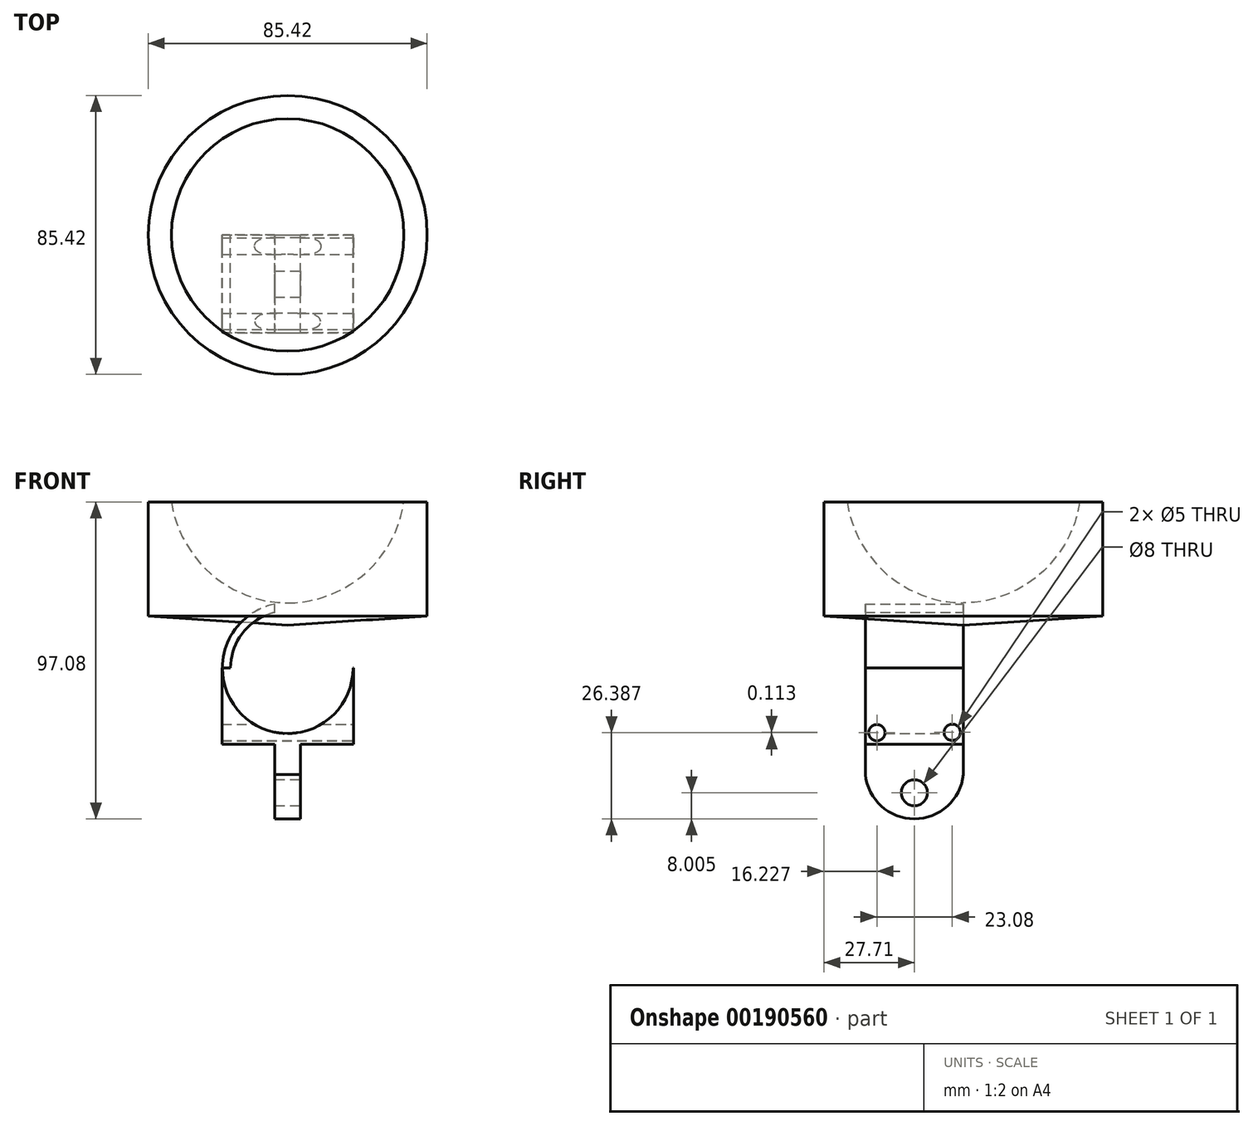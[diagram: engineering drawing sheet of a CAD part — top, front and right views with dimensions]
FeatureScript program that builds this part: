
annotation { "Feature Type Name" : "Feature", "Feature Type Description" : "" }
export const myFeature = defineFeature(function(context is Context, id is Id, definition is map)
    precondition{}
    {
        {
            var Q0;
            Q0=qCreatedBy(makeId("Front.planeOp"),FACE);
            var sketch = newSketch(context, id + "F0", { "sketchPlane" : qUnion([Q0])});
            skCircle(sketch, "E0", {"center": v(0, 0) * mm, "radius": 17.5 * mm});
            skLineSegment(sketch, "E1.bottom", {"start": v(3.9, -46.27) * mm, "end": v(-3.9, -46.27) * mm});
            skLineSegment(sketch, "E1.top", {"start": v(3.9, 46.27) * mm, "end": v(-3.9, 46.27) * mm});
            skLineSegment(sketch, "E1.left", {"start": v(3.9, -46.27) * mm, "end": v(3.9, 46.27) * mm});
            skLineSegment(sketch, "E1.right", {"start": v(-3.9, -46.27) * mm, "end": v(-3.9, 46.27) * mm});
            skCircle(sketch, "E2", {"center": v(0, 0) * mm, "radius": 20 * mm});
            skLineSegment(sketch, "E3.bottom", {"start": v(20.14, -23.25) * mm, "end": v(-20.14, -23.25) * mm});
            skLineSegment(sketch, "E3.top", {"start": v(20.14, 23.25) * mm, "end": v(-20.14, 23.25) * mm});
            skLineSegment(sketch, "E3.left", {"start": v(20.14, -23.25) * mm, "end": v(20.14, 23.25) * mm});
            skLineSegment(sketch, "E3.right", {"start": v(-20.14, -23.25) * mm, "end": v(-20.14, 23.25) * mm});
            skLineSegment(sketch, "E4", {"start": v(-17.5, 0) * mm, "end": v(20, 0) * mm});
            skPoint(sketch, "E4.startSnap0", {"position": v(-20.14, 0) * mm});
            skLineSegment(sketch, "E5", {"start": v(-20.14, 0) * mm, "end": v(20, 0) * mm});
            skLineSegment(sketch, "E6", {"start": v(25.02, 0) * mm, "end": v(-25.66, 0) * mm});
            skSolve(sketch);
        }
        {
            var Q0;
            {var subQ1=sQuery(id+"F0.wireOp",EDGE,"E3.bottom");var subQ5=sQuery(id+"F0.wireOp",EDGE,"E1.left");var subQ6=makeQuery(id+"F0.imprint","INTERSECT",VERTEX,{"derivedFrom":[subQ5,subQ1]});Q0=makeQuery(id+"F0.imprint","IMPRINT",FACE,{"disambiguationData":[TD([[makeQuery(id+"F0.imprint","IMPRINT",EDGE,{"disambiguationData":[TD([[subQ6,-1.0]])],"derivedFrom":subQ5}),-1.0]])]});}
            var Q1;
            {var subQ0=sQuery(id+"F0.wireOp",EDGE,"E6");var subQ1=sQuery(id+"F0.wireOp",EDGE,"E0");var subQ2=makeQuery(id+"F0.imprint","INTERSECT",VERTEX,{"disambiguationData":[OD(0.0)],"derivedFrom":[subQ1,subQ0]});Q1=makeQuery(id+"F0.imprint","IMPRINT",FACE,{"disambiguationData":[TD([[makeQuery(id+"F0.imprint","IMPRINT",EDGE,{"disambiguationData":[TD([[subQ2,1.0]])],"derivedFrom":subQ1}),-1.0]])]});}
            var Q2;
            {var subQ0=sQuery(id+"F0.wireOp",EDGE,"E1.right");var subQ1=sQuery(id+"F0.wireOp",EDGE,"E0");var subQ2=makeQuery(id+"F0.imprint","INTERSECT",VERTEX,{"disambiguationData":[OD(1.0)],"derivedFrom":[subQ1,subQ0]});Q2=makeQuery(id+"F0.imprint","IMPRINT",FACE,{"disambiguationData":[TD([[makeQuery(id+"F0.imprint","IMPRINT",EDGE,{"disambiguationData":[TD([[subQ2,-1.0]])],"derivedFrom":subQ1}),-1.0]])]});}
            var Q3;
            {var subQ0=sQuery(id+"F0.wireOp",EDGE,"E6");var subQ1=sQuery(id+"F0.wireOp",EDGE,"E0");var subQ2=makeQuery(id+"F0.imprint","INTERSECT",VERTEX,{"disambiguationData":[OD(1.0)],"derivedFrom":[subQ1,subQ0]});Q3=makeQuery(id+"F0.imprint","IMPRINT",FACE,{"disambiguationData":[TD([[makeQuery(id+"F0.imprint","IMPRINT",EDGE,{"disambiguationData":[TD([[subQ2,-1.0]])],"derivedFrom":subQ1}),-1.0]])]});}
            var Q4;
            {var subQ1=sQuery(id+"F0.wireOp",EDGE,"E1.right");var subQ6=sQuery(id+"F0.wireOp",EDGE,"E3.bottom");var subQ9=makeQuery(id+"F0.imprint","INTERSECT",VERTEX,{"derivedFrom":[subQ1,subQ6]});Q4=makeQuery(id+"F0.imprint","IMPRINT",FACE,{"disambiguationData":[TD([[makeQuery(id+"F0.imprint","IMPRINT",EDGE,{"disambiguationData":[TD([[subQ9,-1.0]])],"derivedFrom":subQ1}),1.0]])]});}
            var Q5;
            {var subQ0=sQuery(id+"F0.wireOp",EDGE,"E3.bottom");var subQ1=sQuery(id+"F0.wireOp",EDGE,"E1.left");var subQ2=makeQuery(id+"F0.imprint","INTERSECT",VERTEX,{"derivedFrom":[subQ1,subQ0]});Q5=makeQuery(id+"F0.imprint","IMPRINT",FACE,{"disambiguationData":[TD([[makeQuery(id+"F0.imprint","IMPRINT",EDGE,{"disambiguationData":[TD([[subQ2,-1.0]])],"derivedFrom":subQ1}),1.0]])]});}
            var Q6;
            {var subQ0=sQuery(id+"F0.wireOp",EDGE,"E1.bottom");Q6=makeQuery(id+"F0.imprint","IMPRINT",FACE,{"disambiguationData":[TD([[makeQuery(id+"F0.imprint","IMPRINT",EDGE,{"derivedFrom":subQ0}),-1.0]])]});}
            extrude(context, id + "F1", {"entities" : qUnion([Q0, Q1, Q2, Q3, Q4, Q5, Q6]), "depth" : 30 * mm});
        }
        {
            var Q0;
            Q0=makeQuery(id+"F1.opExtrude","SWEPT_FACE",FACE,{"disambiguationData":[OSD([sQuery(id+"F0.wireOp",EDGE,"E1.left")])]});
            var sketch = newSketch(context, id + "F2", { "sketchPlane" : qUnion([Q0])});
            skCircle(sketch, "E7", {"center": v(-15, -31.08) * mm, "radius": 15.07 * mm});
            skSolve(sketch);
        }
        {
            var Q0;
            {var subQ1=sQuery(id+"F0.wireOp",EDGE,"E1.left");var subQ6=makeQuery(id+"F1.opExtrude","SWEPT_EDGE",EDGE,{"disambiguationData":[OSD([sQuery(id+"F0.wireOp",EDGE,"E1.bottom"),subQ1])]});Q0=makeQuery(id+"F2.imprint","IMPRINT",FACE,{"disambiguationData":[TD([[makeQuery(id+"F2.imprint","IMPRINT",EDGE,{"derivedFrom":subQ6}),1.0]])]});}
            extrude(context, id + "F3", {"entities" : qUnion([Q0]), "operationType" : NewBodyOperationType.REMOVE, "endBound" : BoundingType.THROUGH_ALL, "oppositeDirection" : true, "depth" : 25.4 * mm});
        }
        {
            var Q0;
            Q0=makeQuery(id+"F1.opExtrude","SWEPT_FACE",FACE,{"disambiguationData":[OSD([sQuery(id+"F0.wireOp",EDGE,"E1.left")])]});
            var sketch = newSketch(context, id + "F4", { "sketchPlane" : qUnion([Q0])});
            skCircle(sketch, "E8", {"center": v(-15, -38.16) * mm, "radius": 4 * mm});
            skPoint(sketch, "E8.centerSnap0", {"position": v(-15, -46.16) * mm});
            skCircle(sketch, "E9", {"center": v(-26.48, -19.77) * mm, "radius": 2.5 * mm});
            skCircle(sketch, "E10", {"center": v(-3.4, -19.66) * mm, "radius": 2.5 * mm});
            skSolve(sketch);
        }
        {
            var Q0;
            Q0 = qSketchRegion(id + "F4", true);
            var Q1;
            Q1=sQuery(id+"F4.wireOp",EDGE,"E9");
            var Q2;
            Q2=sQuery(id+"F4.wireOp",EDGE,"E8");
            var Q3;
            Q3=sQuery(id+"F4.wireOp",EDGE,"E10");
            extrude(context, id + "F5", {"entities" : qUnion([Q0]), "operationType" : NewBodyOperationType.REMOVE, "surfaceEntities" : qUnion([Q1, Q2, Q3]), "endBound" : BoundingType.THROUGH_ALL, "oppositeDirection" : true, "depth" : 25.4 * mm, "hasSecondDirection" : true, "secondDirectionBound" : BoundingType.THROUGH_ALL, "secondDirectionOppositeDirection" : false, "secondDirectionDepth" : 25.4 * mm});
        }
        {
            var Q0;
            Q0=qCreatedBy(makeId("Front.planeOp"),FACE);
            var sketch = newSketch(context, id + "F6", { "sketchPlane" : qUnion([Q0])});
            skArc(sketch, "E11", {"start": v(-35.6, 50.92) * mm, "mid": v(-23.53, 28.85) * mm, "end": v(0, 19.96) * mm});
            skLineSegment(sketch, "E12", {"start": v(-35.6, 50.92) * mm, "end": v(-42.71, 50.92) * mm});
            skLineSegment(sketch, "E13", {"start": v(-42.71, 50.92) * mm, "end": v(-42.71, 15.94) * mm});
            skLineSegment(sketch, "E14", {"start": v(-42.71, 15.94) * mm, "end": v(0, 13.15) * mm});
            skLineSegment(sketch, "E15", {"start": v(0, 13.15) * mm, "end": v(0, 19.96) * mm});
            skSolve(sketch);
        }
        {
            var Q0;
            Q0=makeQuery(id+"F6.imprint","IMPRINT",FACE,{"disambiguationData":[TD([[makeQuery(id+"F6.imprint","IMPRINT",EDGE,{"derivedFrom":sQuery(id+"F6.wireOp",EDGE,"E11")}),-1.0]])]});
            var Q1;
            Q1=sQuery(id+"F6.wireOp",EDGE,"E15");
            revolve(context, id + "F7", {"entities" : qUnion([Q0]), "axis" : qUnion([Q1]), "revolveType" : RevolveType.FULL});
        }
    });
